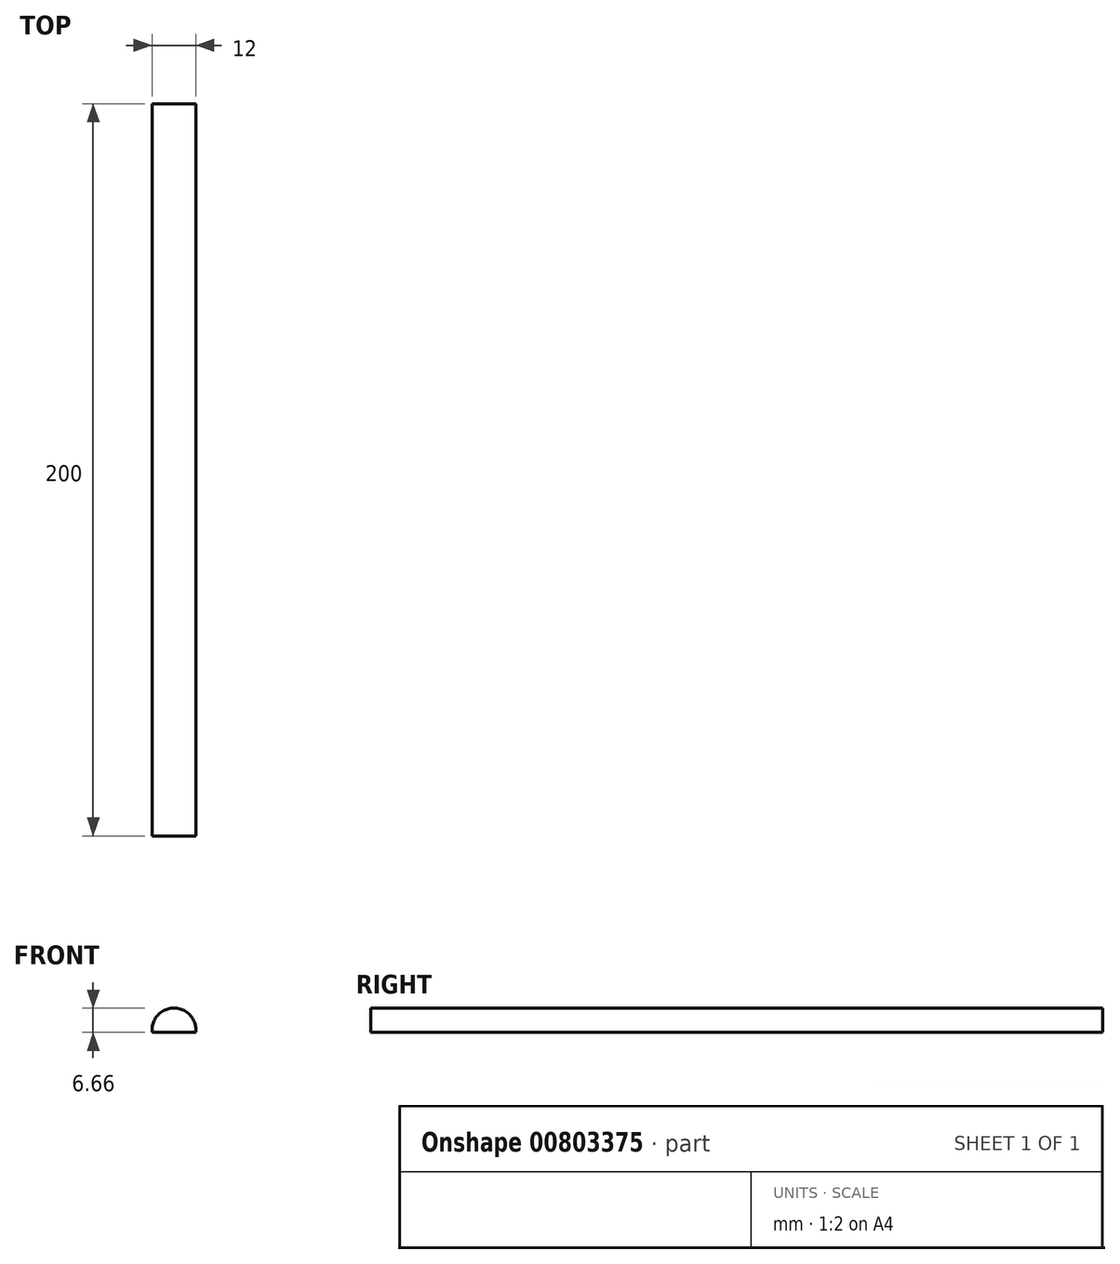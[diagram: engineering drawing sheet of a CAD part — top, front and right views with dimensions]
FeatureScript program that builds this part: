
annotation { "Feature Type Name" : "Feature", "Feature Type Description" : "" }
export const myFeature = defineFeature(function(context is Context, id is Id, definition is map)
    precondition{}
    {
        {
            var Q0;
            Q0=qCreatedBy(makeId("Front.planeOp"),FACE);
            var sketch = newSketch(context, id + "F0", { "sketchPlane" : qUnion([Q0])});
            skArc(sketch, "E0", {"start": v(11.93, 0) * mm, "mid": v(5.96, 6.66) * mm, "end": v(0, 0) * mm});
            skLineSegment(sketch, "E1", {"start": v(11.93, 0) * mm, "end": v(0, 0) * mm});
            skSolve(sketch);
        }
        {
            var Q0;
            Q0=makeQuery(id+"F0.imprint","IMPRINT",FACE,{"disambiguationData":[TD([[makeQuery(id+"F0.imprint","IMPRINT",EDGE,{"derivedFrom":sQuery(id+"F0.wireOp",EDGE,"E0")}),1.0]])]});
            extrude(context, id + "F1", {"entities" : qUnion([Q0]), "depth" : 200 * mm, "offsetDistance" : 25.4 * mm});
        }
    });
